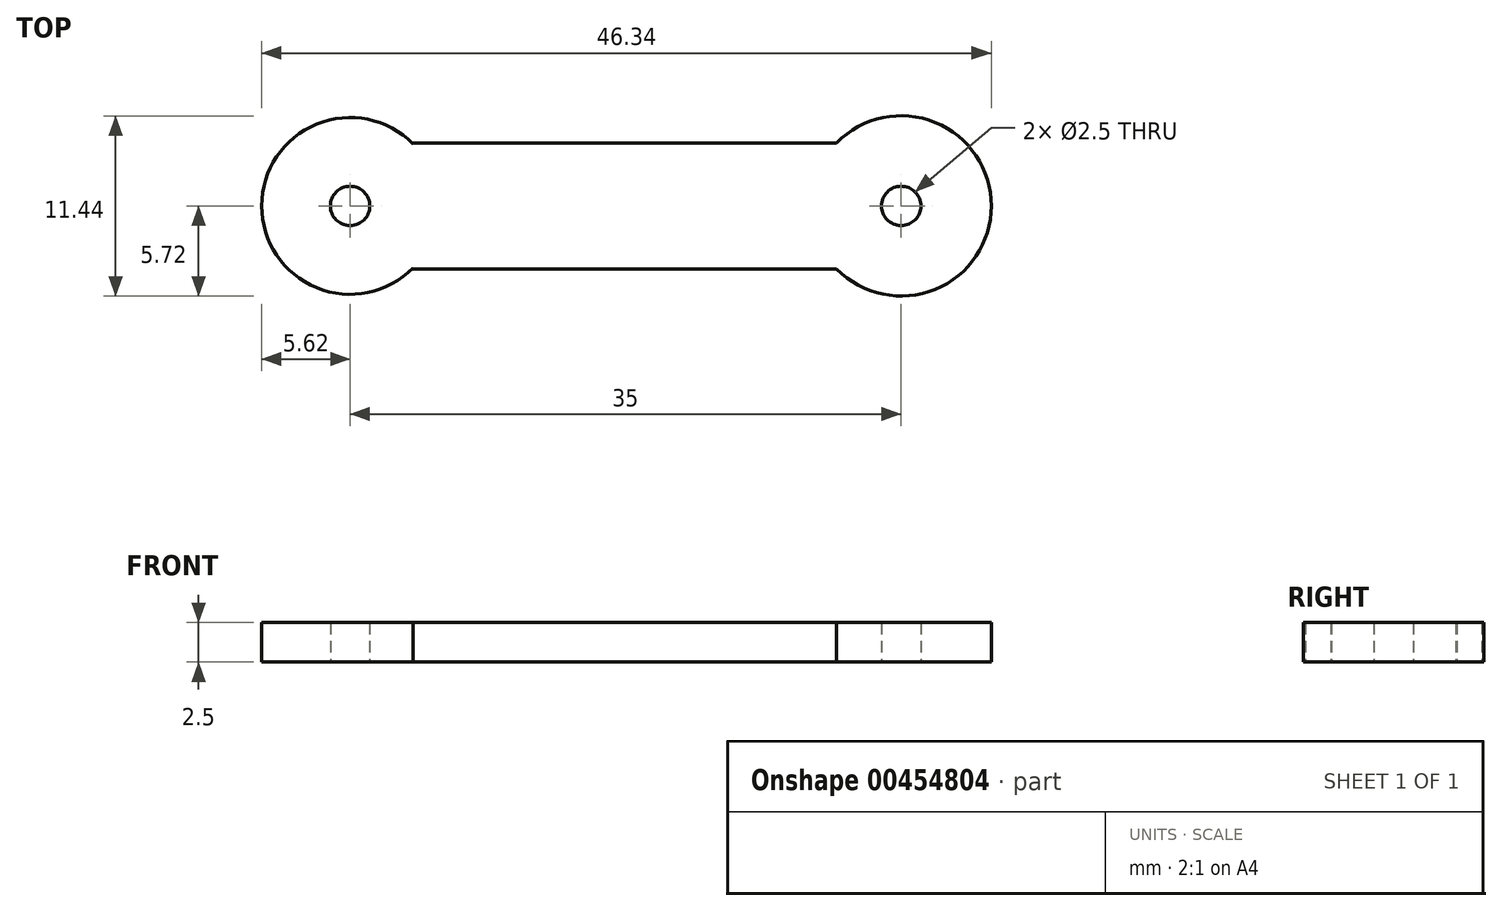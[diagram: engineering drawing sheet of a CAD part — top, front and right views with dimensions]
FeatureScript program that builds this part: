
annotation { "Feature Type Name" : "Feature", "Feature Type Description" : "" }
export const myFeature = defineFeature(function(context is Context, id is Id, definition is map)
    precondition{}
    {
        {
            var Q0;
            Q0=qCreatedBy(makeId("Top.planeOp"),FACE);
            var sketch = newSketch(context, id + "F0", { "sketchPlane" : qUnion([Q0])});
            skLineSegment(sketch, "E0", {"start": v(0, 0) * mm, "end": v(-27, 0) * mm});
            skLineSegment(sketch, "E1", {"start": v(-27, 0) * mm, "end": v(-27, -8) * mm});
            skLineSegment(sketch, "E2", {"start": v(-27, -8) * mm, "end": v(0, -8) * mm});
            skLineSegment(sketch, "E3", {"start": v(0, -8) * mm, "end": v(0, 0) * mm});
            skLineSegment(sketch, "E4", {"start": v(-27, -4) * mm, "end": v(-31, -4) * mm});
            skLineSegment(sketch, "E5", {"start": v(0, -4) * mm, "end": v(4, -4) * mm});
            skCircle(sketch, "E6", {"center": v(4, -4) * mm, "radius": 5.72 * mm});
            skCircle(sketch, "E7", {"center": v(-31, -4) * mm, "radius": 5.62 * mm});
            skCircle(sketch, "E8", {"center": v(-31, -4) * mm, "radius": 1.25 * mm});
            skCircle(sketch, "E9", {"center": v(4, -4) * mm, "radius": 1.25 * mm});
            skSolve(sketch);
        }
        {
            var Q0;
            Q0 = qSketchRegion(id + "F0", true);
            extrude(context, id + "F1", {"entities" : qUnion([Q0]), "depth" : 2.5 * mm});
        }
    });
